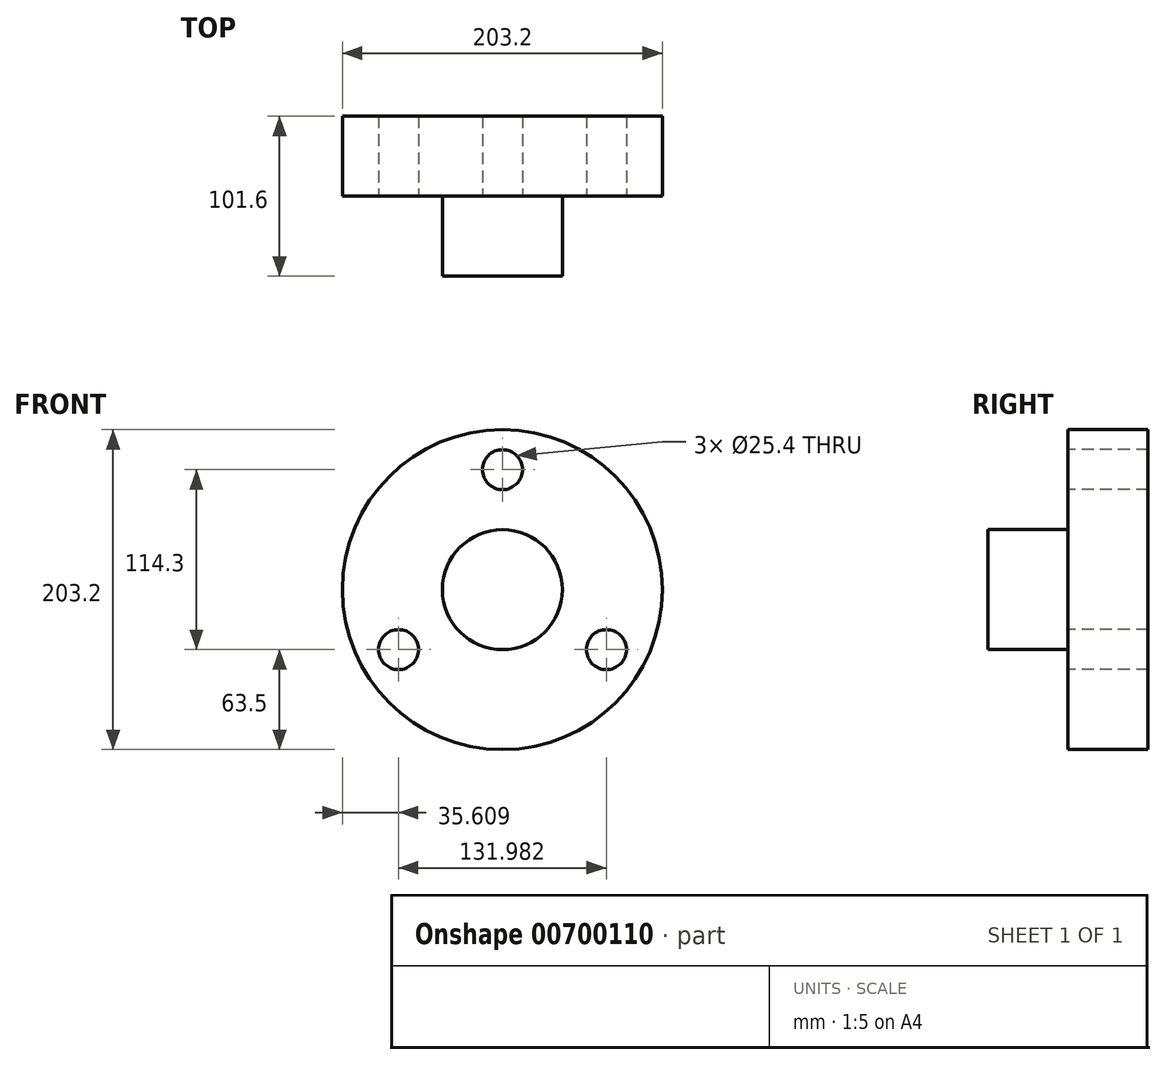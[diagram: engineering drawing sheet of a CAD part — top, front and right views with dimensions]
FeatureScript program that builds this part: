
annotation { "Feature Type Name" : "Feature", "Feature Type Description" : "" }
export const myFeature = defineFeature(function(context is Context, id is Id, definition is map)
    precondition{}
    {
        {
            var Q0;
            Q0=qCreatedBy(makeId("Front.planeOp"),FACE);
            var sketch = newSketch(context, id + "F0", { "sketchPlane" : qUnion([Q0])});
            skCircle(sketch, "E0", {"center": v(0, 0) * mm, "radius": 101.6 * mm});
            skSolve(sketch);
        }
        {
            var Q0;
            Q0 = qSketchRegion(id + "F0", true);
            extrude(context, id + "F1", {"entities" : qUnion([Q0]), "depth" : 50.8 * mm, "offsetDistance" : 25.4 * mm});
        }
        {
            var Q0;
            Q0=makeQuery(id+"F1.opExtrude","CAP_FACE",FACE,{"disambiguationData":[OSD([sQuery(id+"F0.wireOp",EDGE,"E0")])],"isStart":false});
            var sketch = newSketch(context, id + "F2", { "sketchPlane" : qUnion([Q0])});
            skCircle(sketch, "E1", {"center": v(0, 0) * mm, "radius": 38.1 * mm});
            skSolve(sketch);
        }
        {
            var Q0;
            Q0 = qSketchRegion(id + "F2", true);
            extrude(context, id + "F3", {"entities" : qUnion([Q0]), "operationType" : NewBodyOperationType.ADD, "depth" : 50.8 * mm, "offsetDistance" : 25.4 * mm});
        }
        {
            var Q0;
            Q0=makeQuery(id+"F1.opExtrude","CAP_FACE",FACE,{"disambiguationData":[OSD([sQuery(id+"F0.wireOp",EDGE,"E0")])],"isStart":false});
            var sketch = newSketch(context, id + "F4", { "sketchPlane" : qUnion([Q0])});
            skLineSegment(sketch, "E2", {"start": v(0, 0) * mm, "end": v(0, 76.2) * mm, "construction": true});
            skLineSegment(sketch, "E3", {"start": v(0, 0) * mm, "end": v(66, -38.1) * mm, "construction": true});
            skLineSegment(sketch, "E4", {"start": v(0, 0) * mm, "end": v(-66, -38.1) * mm, "construction": true});
            skCircle(sketch, "E5", {"center": v(0, 76.2) * mm, "radius": 12.7 * mm});
            skCircle(sketch, "E6", {"center": v(-66, -38.1) * mm, "radius": 12.7 * mm});
            skPoint(sketch, "E7.center.orphan", {"position": v(66, -40.01) * mm});
            skCircle(sketch, "E8", {"center": v(66, -38.1) * mm, "radius": 12.7 * mm});
            skSolve(sketch);
        }
        {
            var Q0;
            Q0=makeQuery(id+"F4.imprint","IMPRINT",FACE,{"disambiguationData":[TD([[makeQuery(id+"F4.imprint","IMPRINT",EDGE,{"derivedFrom":sQuery(id+"F4.wireOp",EDGE,"E5")}),1.0]])]});
            var Q1;
            Q1=makeQuery(id+"F4.imprint","IMPRINT",FACE,{"disambiguationData":[TD([[makeQuery(id+"F4.imprint","IMPRINT",EDGE,{"derivedFrom":sQuery(id+"F4.wireOp",EDGE,"E6")}),1.0]])]});
            var Q2;
            Q2=makeQuery(id+"F4.imprint","IMPRINT",FACE,{"disambiguationData":[TD([[makeQuery(id+"F4.imprint","IMPRINT",EDGE,{"derivedFrom":sQuery(id+"F4.wireOp",EDGE,"E8")}),1.0]])]});
            extrude(context, id + "F5", {"entities" : qUnion([Q0, Q1, Q2]), "operationType" : NewBodyOperationType.REMOVE, "oppositeDirection" : true, "depth" : 87.38 * mm, "offsetDistance" : 25.4 * mm});
        }
    });
